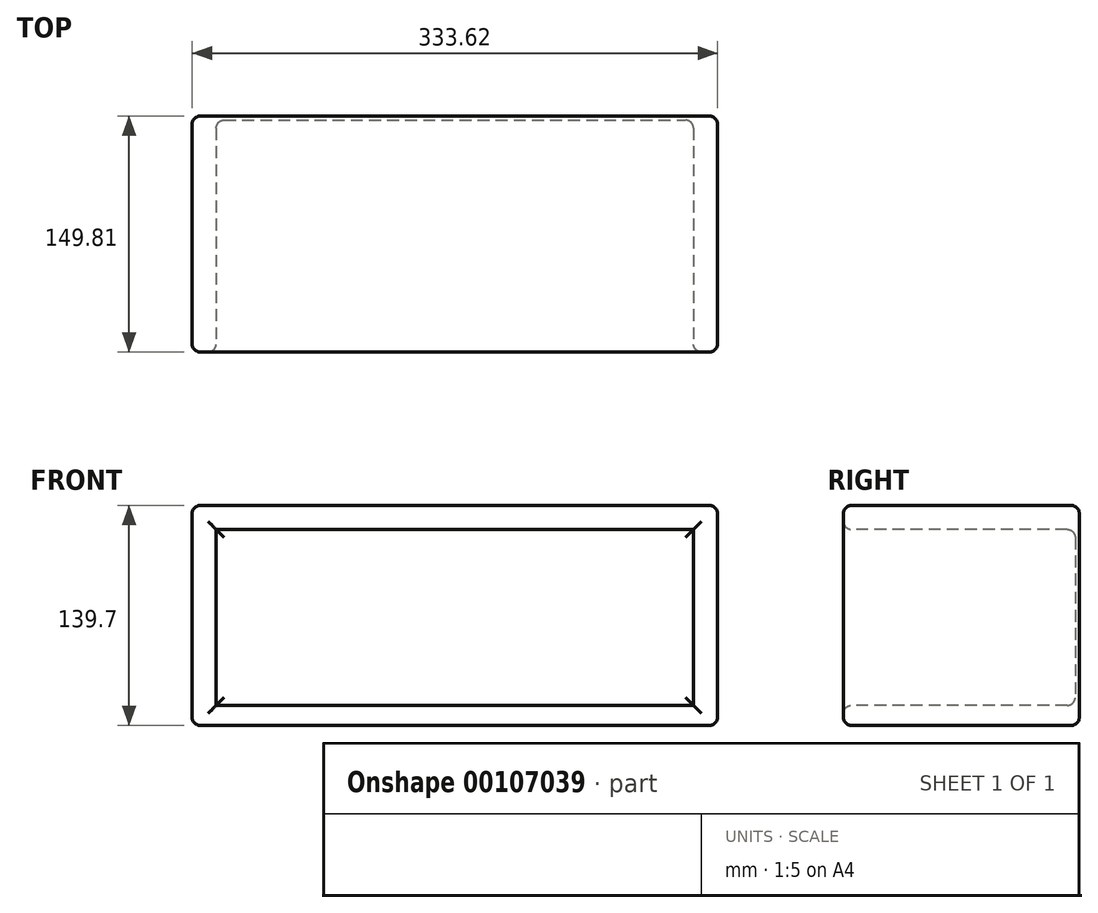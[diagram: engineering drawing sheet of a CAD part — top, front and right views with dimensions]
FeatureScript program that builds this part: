
annotation { "Feature Type Name" : "Feature", "Feature Type Description" : "" }
export const myFeature = defineFeature(function(context is Context, id is Id, definition is map)
    precondition{}
    {
        {
            var Q0;
            Q0=qCreatedBy(makeId("Top.planeOp"),FACE);
            var sketch = newSketch(context, id + "F0", { "sketchPlane" : qUnion([Q0])});
            skLineSegment(sketch, "E0.bottom", {"start": v(-152.73, 73.86) * mm, "end": v(155.5, 73.86) * mm});
            skLineSegment(sketch, "E0.top", {"start": v(-152.73, -75.95) * mm, "end": v(155.5, -75.95) * mm});
            skLineSegment(sketch, "E0.left", {"start": v(-152.73, 73.86) * mm, "end": v(-152.73, -75.95) * mm});
            skLineSegment(sketch, "E0.right", {"start": v(155.5, 73.86) * mm, "end": v(155.5, -75.95) * mm});
            skSolve(sketch);
        }
        {
            var Q0;
            Q0=makeQuery(id+"F0.imprint","IMPRINT",FACE,{"disambiguationData":[TD([[makeQuery(id+"F0.imprint","IMPRINT",EDGE,{"derivedFrom":sQuery(id+"F0.wireOp",EDGE,"E0.bottom")}),-1.0]])]});
            extrude(context, id + "F1", {"entities" : qUnion([Q0]), "depth" : 127 * mm});
        }
        {
            var Q0;
            Q0=makeQuery(id+"F1.opExtrude","CAP_FACE",FACE,{"disambiguationData":[OSD([sQuery(id+"F0.wireOp",EDGE,"E0.bottom"),sQuery(id+"F0.wireOp",EDGE,"E0.top"),sQuery(id+"F0.wireOp",EDGE,"E0.left"),sQuery(id+"F0.wireOp",EDGE,"E0.right")])],"isStart":false});
            var sketch = newSketch(context, id + "F2", { "sketchPlane" : qUnion([Q0])});
            skSolve(sketch);
        }
        {
            var Q0;
            Q0=makeQuery(id+"F1.opExtrude","SWEPT_FACE",FACE,{"disambiguationData":[OSD([sQuery(id+"F0.wireOp",EDGE,"E0.top")])]});
            shell(context, id + "F3", {"entities" : qUnion([Q0]), "thickness" : 2.54 * mm});
        }
        {
            var Q0;
            Q0=makeQuery(id+"F2.imprint","IMPRINT",FACE,{"disambiguationData":[TD([[makeQuery(id+"F2.imprint","IMPRINT",EDGE,{"derivedFrom":makeQuery(id+"F1.opExtrude","CAP_EDGE",EDGE,{"disambiguationData":[OSD([sQuery(id+"F0.wireOp",EDGE,"E0.bottom")])],"isStart":false})}),-1.0]])]});
            extrude(context, id + "F4", {"entities" : qUnion([Q0]), "operationType" : NewBodyOperationType.ADD, "depth" : 12.7 * mm});
        }
        {
            var Q0;
            {var subQ0=sQuery(id+"F0.wireOp",EDGE,"E0.right");Q0=makeQuery(id+"F4.boolean.opBoolean","MERGE",FACE,{"derivedFrom":[makeQuery(id+"F1.opExtrude","SWEPT_FACE",FACE,{"disambiguationData":[OSD([subQ0])]}),makeQuery(id+"F4.opExtrude","SWEPT_FACE",FACE,{"disambiguationData":[OSD([subQ0])]})]});}
            extrude(context, id + "F5", {"entities" : qUnion([Q0]), "operationType" : NewBodyOperationType.ADD, "depth" : 12.7 * mm});
        }
        {
            var Q0;
            {var subQ0=sQuery(id+"F0.wireOp",EDGE,"E0.left");Q0=makeQuery(id+"F4.boolean.opBoolean","MERGE",FACE,{"derivedFrom":[makeQuery(id+"F1.opExtrude","SWEPT_FACE",FACE,{"disambiguationData":[OSD([subQ0])]}),makeQuery(id+"F4.opExtrude","SWEPT_FACE",FACE,{"disambiguationData":[OSD([subQ0])]})]});}
            extrude(context, id + "F6", {"entities" : qUnion([Q0]), "operationType" : NewBodyOperationType.ADD, "depth" : 12.7 * mm});
        }
        {
            var Q0;
            Q0=makeQuery(id+"F0.imprint","IMPRINT",FACE,{"disambiguationData":[TD([[makeQuery(id+"F0.imprint","IMPRINT",EDGE,{"derivedFrom":sQuery(id+"F0.wireOp",EDGE,"E0.bottom")}),-1.0]])]});
            extrude(context, id + "F7", {"entities" : qUnion([Q0]), "operationType" : NewBodyOperationType.ADD, "depth" : 12.7 * mm});
        }
        {
            var Q0;
            {var subQ0=sQuery(id+"F0.wireOp",EDGE,"E0.left");Q0=makeQuery(id+"F6.opExtrude","CAP_EDGE",EDGE,{"disambiguationData":[OSD([subQ0]),TDD([makeQuery(id+"F4.opExtrude","CAP_EDGE",EDGE,{"disambiguationData":[OSD([subQ0])],"isStart":false})])],"isStart":false});}
            var Q1;
            {var subQ0=sQuery(id+"F0.wireOp",EDGE,"E0.left");Q1=makeQuery(id+"F6.opExtrude","CAP_EDGE",EDGE,{"disambiguationData":[OSD([subQ0]),TDD([makeQuery(id+"F1.opExtrude","CAP_EDGE",EDGE,{"disambiguationData":[OSD([subQ0])],"isStart":true})])],"isStart":false});}
            var Q2;
            {var subQ0=sQuery(id+"F0.wireOp",EDGE,"E0.right");Q2=makeQuery(id+"F5.opExtrude","CAP_EDGE",EDGE,{"disambiguationData":[OSD([subQ0]),TDD([makeQuery(id+"F4.opExtrude","CAP_EDGE",EDGE,{"disambiguationData":[OSD([subQ0])],"isStart":false})])],"isStart":false});}
            var Q3;
            {var subQ0=sQuery(id+"F0.wireOp",EDGE,"E0.right");Q3=makeQuery(id+"F5.opExtrude","CAP_EDGE",EDGE,{"disambiguationData":[OSD([subQ0]),TDD([makeQuery(id+"F1.opExtrude","CAP_EDGE",EDGE,{"disambiguationData":[OSD([subQ0])],"isStart":true})])],"isStart":false});}
            fillet(context, id + "F8", {"entities" : qUnion([Q0, Q1, Q2, Q3]), "radius" : 5.08 * mm, "tangentPropagation" : true, "allowEdgeOverflow" : false});
        }
        {
            var Q0;
            {var subQ0=sQuery(id+"F0.wireOp",EDGE,"E0.left");var subQ1=sQuery(id+"F0.wireOp",EDGE,"E0.bottom");var subQ2=sQuery(id+"F0.wireOp",EDGE,"E0.right");Q0=makeQuery(id+"F6.boolean.opBoolean","MERGE",EDGE,{"derivedFrom":[makeQuery(id+"F5.boolean.opBoolean","MERGE",EDGE,{"derivedFrom":[makeQuery(id+"F4.opExtrude","CAP_EDGE",EDGE,{"disambiguationData":[OSD([subQ1])],"isStart":false}),makeQuery(id+"F5.opExtrude","SWEPT_EDGE",EDGE,{"disambiguationData":[OSD([subQ1,subQ2]),TDD([makeQuery(id+"F4.opExtrude","CAP_VERTEX",VERTEX,{"disambiguationData":[OSD([subQ1,subQ2])],"isStart":false})])]})]}),makeQuery(id+"F6.opExtrude","SWEPT_EDGE",EDGE,{"disambiguationData":[OSD([subQ1,subQ0]),TDD([makeQuery(id+"F4.opExtrude","CAP_VERTEX",VERTEX,{"disambiguationData":[OSD([subQ1,subQ0])],"isStart":false})])]})]});}
            fillet(context, id + "F9", {"entities" : qUnion([Q0]), "radius" : 5.08 * mm, "tangentPropagation" : true, "allowEdgeOverflow" : false});
        }
        {
            var Q0;
            Q0=makeQuery(id+"F3.opShell","OFFSET_EDGE",EDGE,{"disambiguationData":[OSD([sQuery(id+"F0.wireOp",EDGE,"E0.top"),sQuery(id+"F0.wireOp",EDGE,"E0.left")])]});
            var Q1;
            Q1=makeQuery(id+"F7.opExtrude","CAP_EDGE",EDGE,{"disambiguationData":[OSD([sQuery(id+"F0.wireOp",EDGE,"E0.top")])],"isStart":false});
            var Q2;
            {var subQ0=sQuery(id+"F0.wireOp",EDGE,"E0.top");Q2=makeQuery(id+"F3.opShell","OFFSET_EDGE",EDGE,{"disambiguationData":[OSD([subQ0]),TDD([makeQuery(id+"F1.opExtrude","CAP_EDGE",EDGE,{"disambiguationData":[OSD([subQ0])],"isStart":false})])]});}
            var Q3;
            Q3=makeQuery(id+"F3.opShell","OFFSET_EDGE",EDGE,{"disambiguationData":[OSD([sQuery(id+"F0.wireOp",EDGE,"E0.top"),sQuery(id+"F0.wireOp",EDGE,"E0.right")])]});
            fillet(context, id + "F10", {"entities" : qUnion([Q0, Q1, Q2, Q3]), "radius" : 5.08 * mm, "tangentPropagation" : true, "allowEdgeOverflow" : false});
        }
        {
            var Q0;
            {var subQ0=sQuery(id+"F0.wireOp",EDGE,"E0.left");var subQ1=sQuery(id+"F0.wireOp",EDGE,"E0.top");var subQ2=sQuery(id+"F0.wireOp",EDGE,"E0.right");Q0=makeQuery(id+"F6.boolean.opBoolean","MERGE",EDGE,{"derivedFrom":[makeQuery(id+"F5.boolean.opBoolean","MERGE",EDGE,{"derivedFrom":[makeQuery(id+"F4.opExtrude","CAP_EDGE",EDGE,{"disambiguationData":[OSD([subQ1])],"isStart":false}),makeQuery(id+"F5.opExtrude","SWEPT_EDGE",EDGE,{"disambiguationData":[OSD([subQ1,subQ2]),TDD([makeQuery(id+"F4.opExtrude","CAP_VERTEX",VERTEX,{"disambiguationData":[OSD([subQ1,subQ2])],"isStart":false})])]})]}),makeQuery(id+"F6.opExtrude","SWEPT_EDGE",EDGE,{"disambiguationData":[OSD([subQ1,subQ0]),TDD([makeQuery(id+"F4.opExtrude","CAP_VERTEX",VERTEX,{"disambiguationData":[OSD([subQ1,subQ0])],"isStart":false})])]})]});}
            fillet(context, id + "F11", {"entities" : qUnion([Q0]), "radius" : 5.08 * mm, "tangentPropagation" : true, "allowEdgeOverflow" : false});
        }
        {
            var Q0;
            {var subQ0=sQuery(id+"F0.wireOp",EDGE,"E0.bottom");Q0=makeQuery(id+"F7.boolean.opBoolean","INTERSECT",EDGE,{"derivedFrom":[makeQuery(id+"F3.opShell","OFFSET_FACE",FACE,{"disambiguationData":[OSD([subQ0])]}),makeQuery(id+"F7.opExtrude","CAP_FACE",FACE,{"disambiguationData":[OSD([subQ0,sQuery(id+"F0.wireOp",EDGE,"E0.top"),sQuery(id+"F0.wireOp",EDGE,"E0.left"),sQuery(id+"F0.wireOp",EDGE,"E0.right")])],"isStart":false})]});}
            var Q1;
            Q1=makeQuery(id+"F3.opShell","OFFSET_EDGE",EDGE,{"disambiguationData":[OSD([sQuery(id+"F0.wireOp",EDGE,"E0.bottom"),sQuery(id+"F0.wireOp",EDGE,"E0.left")])]});
            var Q2;
            {var subQ0=sQuery(id+"F0.wireOp",EDGE,"E0.bottom");Q2=makeQuery(id+"F3.opShell","OFFSET_EDGE",EDGE,{"disambiguationData":[OSD([subQ0]),TDD([makeQuery(id+"F1.opExtrude","CAP_EDGE",EDGE,{"disambiguationData":[OSD([subQ0])],"isStart":false})])]});}
            var Q3;
            Q3=makeQuery(id+"F3.opShell","OFFSET_EDGE",EDGE,{"disambiguationData":[OSD([sQuery(id+"F0.wireOp",EDGE,"E0.bottom"),sQuery(id+"F0.wireOp",EDGE,"E0.right")])]});
            fillet(context, id + "F12", {"entities" : qUnion([Q0, Q1, Q2, Q3]), "radius" : 5.08 * mm, "tangentPropagation" : true, "allowEdgeOverflow" : false});
        }
    });
